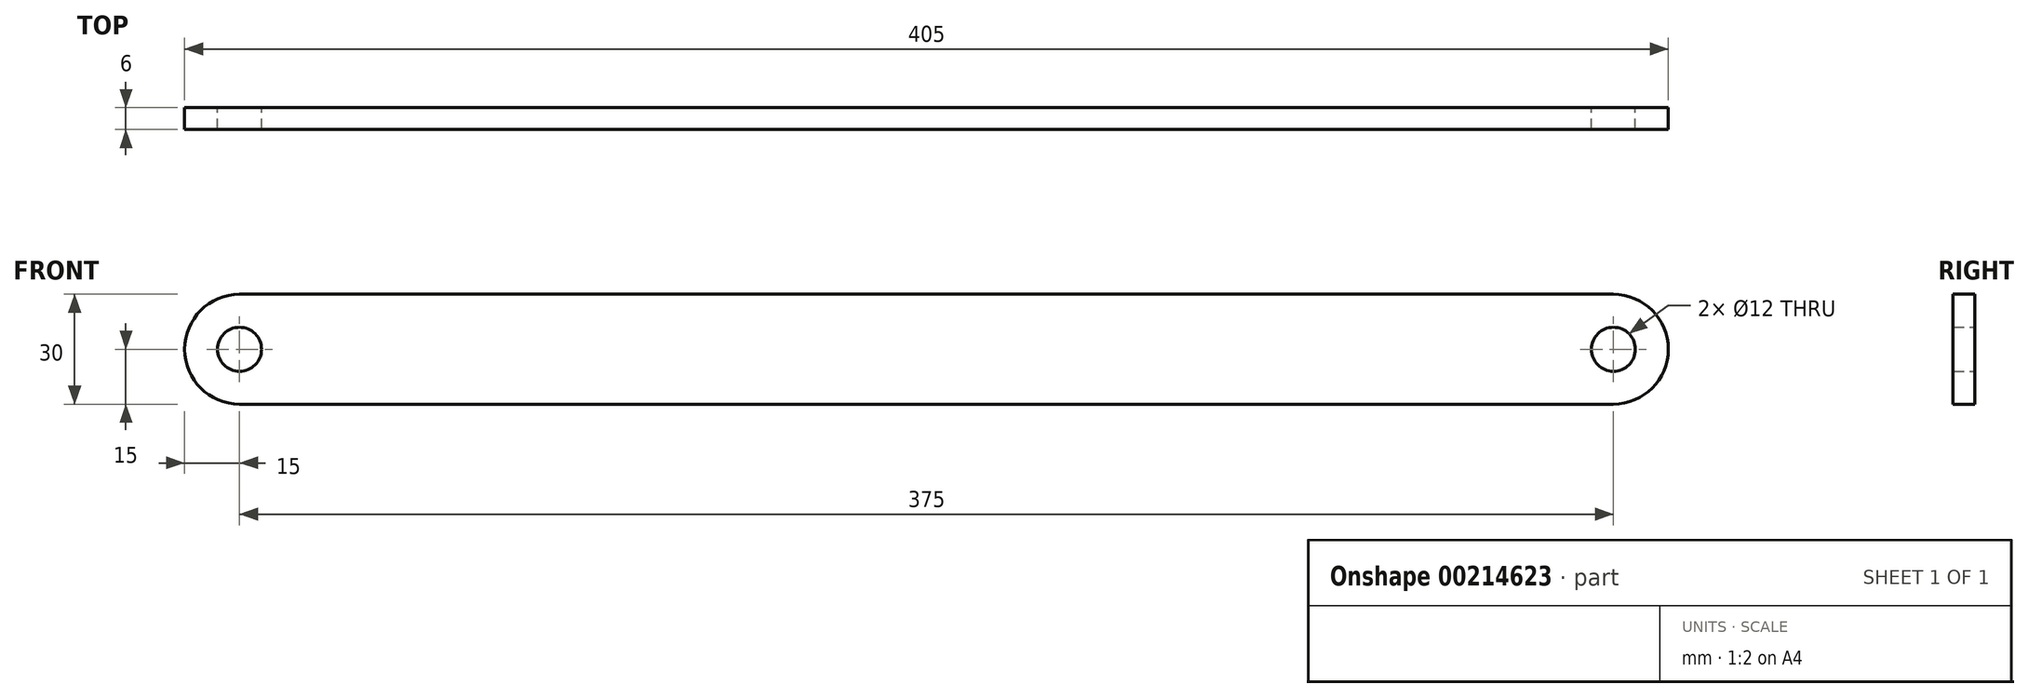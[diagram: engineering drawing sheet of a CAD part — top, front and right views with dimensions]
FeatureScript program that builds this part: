
annotation { "Feature Type Name" : "Feature", "Feature Type Description" : "" }
export const myFeature = defineFeature(function(context is Context, id is Id, definition is map)
    precondition{}
    {
        {
            var Q0;
            Q0=qCreatedBy(makeId("Front.planeOp"),FACE);
            var sketch = newSketch(context, id + "F0", { "sketchPlane" : qUnion([Q0])});
            skCircle(sketch, "E0", {"center": v(0, 0) * mm, "radius": 6 * mm});
            skCircle(sketch, "E1", {"center": v(375, 0) * mm, "radius": 6 * mm});
            skArc(sketch, "E2", {"start": v(0, 15) * mm, "mid": v(-15, 0) * mm, "end": v(0, -15) * mm});
            skArc(sketch, "E3", {"start": v(375, -15) * mm, "mid": v(390, 0) * mm, "end": v(375, 15) * mm});
            skLineSegment(sketch, "E4", {"start": v(0, 15) * mm, "end": v(375, 15) * mm});
            skLineSegment(sketch, "E5", {"start": v(375, -15) * mm, "end": v(0, -15) * mm});
            skSolve(sketch);
        }
        {
            var Q0;
            Q0=makeQuery(id+"F0.imprint","IMPRINT",FACE,{"disambiguationData":[TD([[makeQuery(id+"F0.imprint","IMPRINT",EDGE,{"derivedFrom":sQuery(id+"F0.wireOp",EDGE,"E0")}),-1.0]])]});
            extrude(context, id + "F1", {"entities" : qUnion([Q0]), "depth" : 6 * mm});
        }
    });
